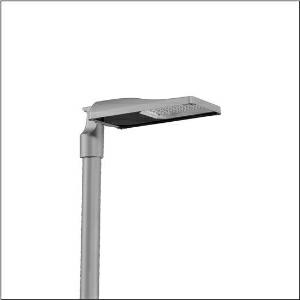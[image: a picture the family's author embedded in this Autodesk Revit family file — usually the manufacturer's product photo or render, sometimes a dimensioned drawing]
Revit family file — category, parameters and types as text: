
# Revit family: streetlight_sl_31_mini___st1_0a_5xh2d71b08ha_8b0a
name_source: partatom
category: Lighting Fixtures
units: mm (PartAtom-declared; Revit-internal decimal feet)

## family parameters
Cut with Voids When Loaded = No
Host = Face
Light Source = No
Part Type = Normal
Room Calculation Point = No
Round Connector Dimension = Use Diameter
Shared = No

## types (1)
- --- (1 x LED, 7620 lm, 68.3 W, 2200K)
    Apparent Load = 68 VA
    CIE Flux Codes = 37 72 97 100 100
    Color Rendering = 70
    Color Temperature = 2200K
    Default Elevation = 1800 mm
    Description = Streetlight SL 31 mini Easy, LST, Desk-Remote mast luminaire for post-top, side-entry; light control with lens of PMMA; light distribution: ST1.0a, direct asymmetric distribution, for standard-compliant lighting for roads and squares; LED: luminous flux: 7.620lm, light colour: 722, colour temperature: 2200K; luminous efficacy: 111,6lm/W; control: pre-setting: linear dimming characteristic, flexible luminous flux parameterisation, time-dependent luminous flux control, constant luminous flux control, power reduction, intelligent temperature release in ECG and LED module, overheat protection; luminaire housing, of diecast aluminium, Siteco® metallic grey (DB 702S), corrosivity category C5 high according to DIN EN ISO 12944; cover of toughened safety glass, transparent, mast flange of diecast aluminium, Siteco® metallic grey (DB 702S), spigot size: 76/60mm, mast flange included unmounted; with cable H07RN-F 3x 1.5mm², cable length: 8,5m, connection cable pre-assembled; mains connection: 220..240V, AC, 50/60Hz; power consumption (at start of service life): 68,3W / (at end of service life): 74,8W / (with reduced operation 50%): 29,4W; protection rating (complete): IP66; insulation class (complete): insulation class II (safety insulation); impact resistance: IK10; certification: CE, ENEC, ENEC+, VDE, UKCA; permissible operating ambient temperature for outdoor applications: -40..+50°C; packaging unit: 1 piece

Light Distribution: ST1.0a
    Height = 76 mm
    Lamp = 1 x LED
    Lamp Light Flux = 7620 lm
    Lamp Power = 68.3 W
    Lamp count = 1
    Length = 547 mm
    Luminous efficacy = 112 lm/W
    Manufacturer = Siteco
    ModVariant = No
    Model = 5XH2D71B08HA
    Number of Poles = 1
    OnlyDefault = Yes
    Power Factor = 1
    Product Name = Streetlight SL 31 mini | ST1.0a
    Product group = mast luminaire | pylon top
    ProductGroupID = 6100
    Protection Class = Protection class II
    Protection Degree = IP 66
    RLX_Detail_Level = 1
    RLX_Emergency_Light_Flux = 0 lm
    RLX_Emergency_Type = 0
    RLX_Emergency_Type_DB = No
    RlxData = <blob elided: 39421 chars, md5=a8376052>
    Socket = socket
    Standby Power = 0 W
    System Light Flux = 7620 lm
    System Power = 68 W
    Type Comments = factory setting: luminous flux: 100 % | dim-lin: 254 | 693 mA
    Type Image = l_1300326.jpg
    URL = http://relux.com
    VarID = @adj_054982
    Voltage = 0 V
    Weight = 0.00 kg
    Width = 265 mm

## geometry (parser evidence)
native form markers: Blend x4, Sweep x9
no freeform markers — native parametric forms only
